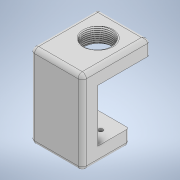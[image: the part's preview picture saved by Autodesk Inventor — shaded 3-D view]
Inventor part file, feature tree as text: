
AUTODESK INVENTOR PART (.ipt)
format: ipt  version: 2021 (Build 250183000, 183)  size: 529,920 bytes
history: native  units: in
note: dims shown in document units (in); Inventor stores cm internally (conversion verified against a paired STEP export)
features: sketch x8, extrude x7, projected_geometry x4, fillet x3, chamfer x1, plane x1, other x1, helix x1
ambient origin geometry x8: Origin, YZ Plane, XZ Plane, XY Plane, X Axis, Y Axis, Z Axis, Center Point
bodies: Solid1 (feature_tree)
feature tree (26):
  extrude  "Extrusion1"  Depth=0.5906in
  extrude  "Extrusion2"  Depth=1.9685in
  extrude  "Extrusion3"  Depth=1.1811in TaperAngle=0.0deg
  chamfer  "Chamfer1"  Distance=1.1811in
  fillet  "Fillet1"  Radius=0.1575in
  extrude  "Extrusion4"  Depth=0.5906in TaperAngle=0.0deg
  extrude  "Extrusion5"  Depth=0.5906in
  extrude  "Extrusion6"  Depth=1.9685in TaperAngle=0.0deg
  sketch  "Sketch7"  dims[d13=0.0787in d14=0.0787in d15=45.0deg d16=0.1575in]
  fillet  "Fillet2"  Radius=0.1575in
  extrude  "Extrusion7"  Depth=0.9843in
  plane  "Work Plane2"
  sketch  "Sketch8"  dims[d17=0.9094in d18=0.0in d19=0.5906in d20=0.0in d21=0.5906in d22=1.9685in d23=0.0in d31=0.1575in d32=0.9843in d33=0.9843in d34=1.063in d35=1.9685in d36=0.0in d37=-0.9843in d38=0.0787in d39=0.0295in d40=0.0787in d41=0.0079in d42=0.0669in d43=2.2343in d44=0.3937in d45=0.0in d46=90.0deg d47=90.0deg d48=0.0in d49=0.0in d52=0.0787in]
  other  "Work Axis1"
  helix  "Coil1"  [1 undecoded]
  fillet  "Fillet3"  Radius=1.063in
  sketch  "Sketch1"  dims[d0=1.6811in d1=0.5906in]
  sketch  "Sketch2"  dims[d2=3.1496in d3=1.9685in]
  sketch  "Sketch3"  dims[d4=0.5906in d5=0.0in d6=1.1811in d7=0.0in]
  sketch  "Sketch4"  dims[d8=0.1575in]
  sketch  "Sketch5"  dims[d9=0.4724in]
  sketch  "Sketch6"  dims[d10=0.4724in d11=1.1811in d12=0.0in]
  projected_geometry  "Projected Loop1"
  projected_geometry  "Project Cut Edges1"
  projected_geometry  "Project Cut Edges2"
  projected_geometry  "Project Cut Edges3"
note: 1 required parameter value undecoded (feature->parameter linkage not recoverable at this tier; creation-order binding heuristic only, values carry confidence <= 0.55)
